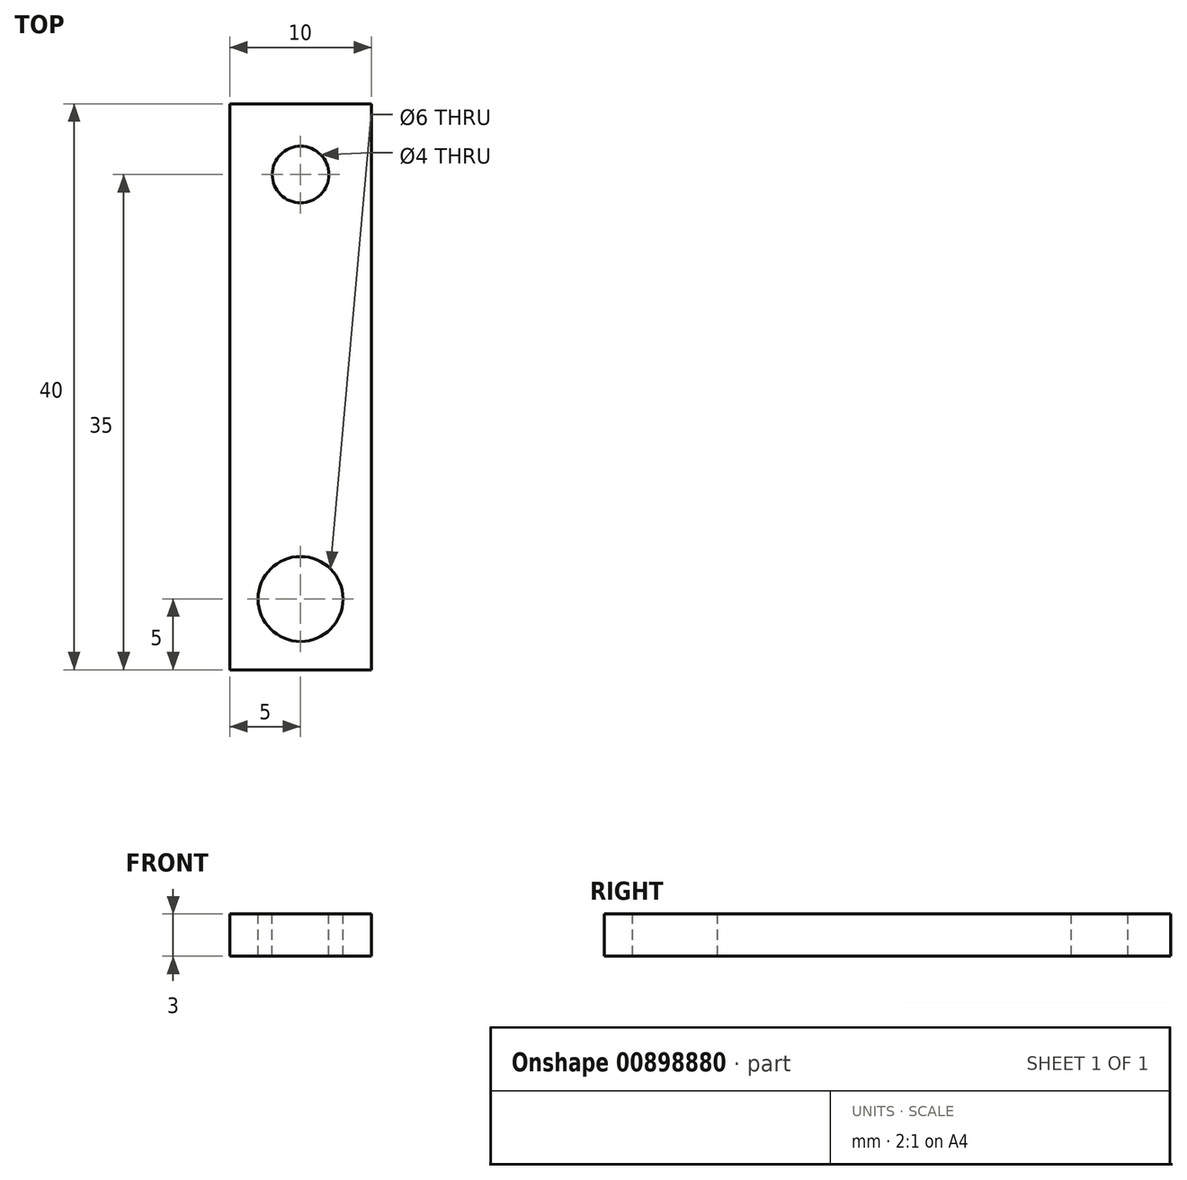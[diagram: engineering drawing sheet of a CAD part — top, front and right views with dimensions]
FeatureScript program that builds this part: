
annotation { "Feature Type Name" : "Feature", "Feature Type Description" : "" }
export const myFeature = defineFeature(function(context is Context, id is Id, definition is map)
    precondition{}
    {
        {
            var Q0;
            Q0=qCreatedBy(makeId("Top.planeOp"),FACE);
            var sketch = newSketch(context, id + "F0", { "sketchPlane" : qUnion([Q0])});
            skLineSegment(sketch, "E0.bottom", {"start": v(0, 0) * mm, "end": v(-10, 0) * mm});
            skLineSegment(sketch, "E0.top", {"start": v(0, 40) * mm, "end": v(-10, 40) * mm});
            skLineSegment(sketch, "E0.left", {"start": v(0, 0) * mm, "end": v(0, 40) * mm});
            skLineSegment(sketch, "E0.right", {"start": v(-10, 0) * mm, "end": v(-10, 40) * mm});
            skSolve(sketch);
        }
        {
            var Q0;
            Q0 = qSketchRegion(id + "F0", true);
            extrude(context, id + "F1", {"entities" : qUnion([Q0]), "depth" : 3 * mm, "offsetDistance" : 25 * mm});
        }
        {
            var Q0;
            Q0=makeQuery(id+"F1.opExtrude","CAP_FACE",FACE,{"disambiguationData":[OSD([sQuery(id+"F0.wireOp",EDGE,"E0.bottom"),sQuery(id+"F0.wireOp",EDGE,"E0.top"),sQuery(id+"F0.wireOp",EDGE,"E0.left"),sQuery(id+"F0.wireOp",EDGE,"E0.right")])],"isStart":false});
            var sketch = newSketch(context, id + "F2", { "sketchPlane" : qUnion([Q0])});
            skPoint(sketch, "E1", {"position": v(-5, 0) * mm});
            skPoint(sketch, "E2", {"position": v(-5, 40) * mm});
            skPoint(sketch, "E3", {"position": v(-5, 5) * mm});
            skPoint(sketch, "E4", {"position": v(-5, 35) * mm});
            skSolve(sketch);
        }
        {
            var Q0;
            Q0=sQuery(id+"F2.wireOp",VERTEX,"E3");
            var Q1;
            Q1=makeQuery(id+"F1.opExtrude","SWEPT_BODY",BODY,{"disambiguationData":[OSD([sQuery(id+"F0.wireOp",EDGE,"E0.bottom"),sQuery(id+"F0.wireOp",EDGE,"E0.top"),sQuery(id+"F0.wireOp",EDGE,"E0.left"),sQuery(id+"F0.wireOp",EDGE,"E0.right")])]});
            hole(context, id + "F3", {"style" : HoleStyle.SIMPLE, "endStyle" : HoleEndStyle.THROUGH, "holeDiameter" : 6 * mm, "majorDiameter" : 5 * mm, "isTappedThrough" : true, "tappedDepth" : 12 * mm, "tapClearance" : 3, "locations" : qUnion([Q0]), "scope" : qUnion([Q1])});
        }
        {
            var Q0;
            Q0=sQuery(id+"F2.wireOp",VERTEX,"E4");
            var Q1;
            Q1=makeQuery(id+"F1.opExtrude","SWEPT_BODY",BODY,{"disambiguationData":[OSD([sQuery(id+"F0.wireOp",EDGE,"E0.bottom"),sQuery(id+"F0.wireOp",EDGE,"E0.top"),sQuery(id+"F0.wireOp",EDGE,"E0.left"),sQuery(id+"F0.wireOp",EDGE,"E0.right")])]});
            hole(context, id + "F4", {"style" : HoleStyle.SIMPLE, "endStyle" : HoleEndStyle.THROUGH, "holeDiameter" : 4 * mm, "majorDiameter" : 5 * mm, "isTappedThrough" : true, "tappedDepth" : 12 * mm, "tapClearance" : 3, "locations" : qUnion([Q0]), "scope" : qUnion([Q1])});
        }
    });
